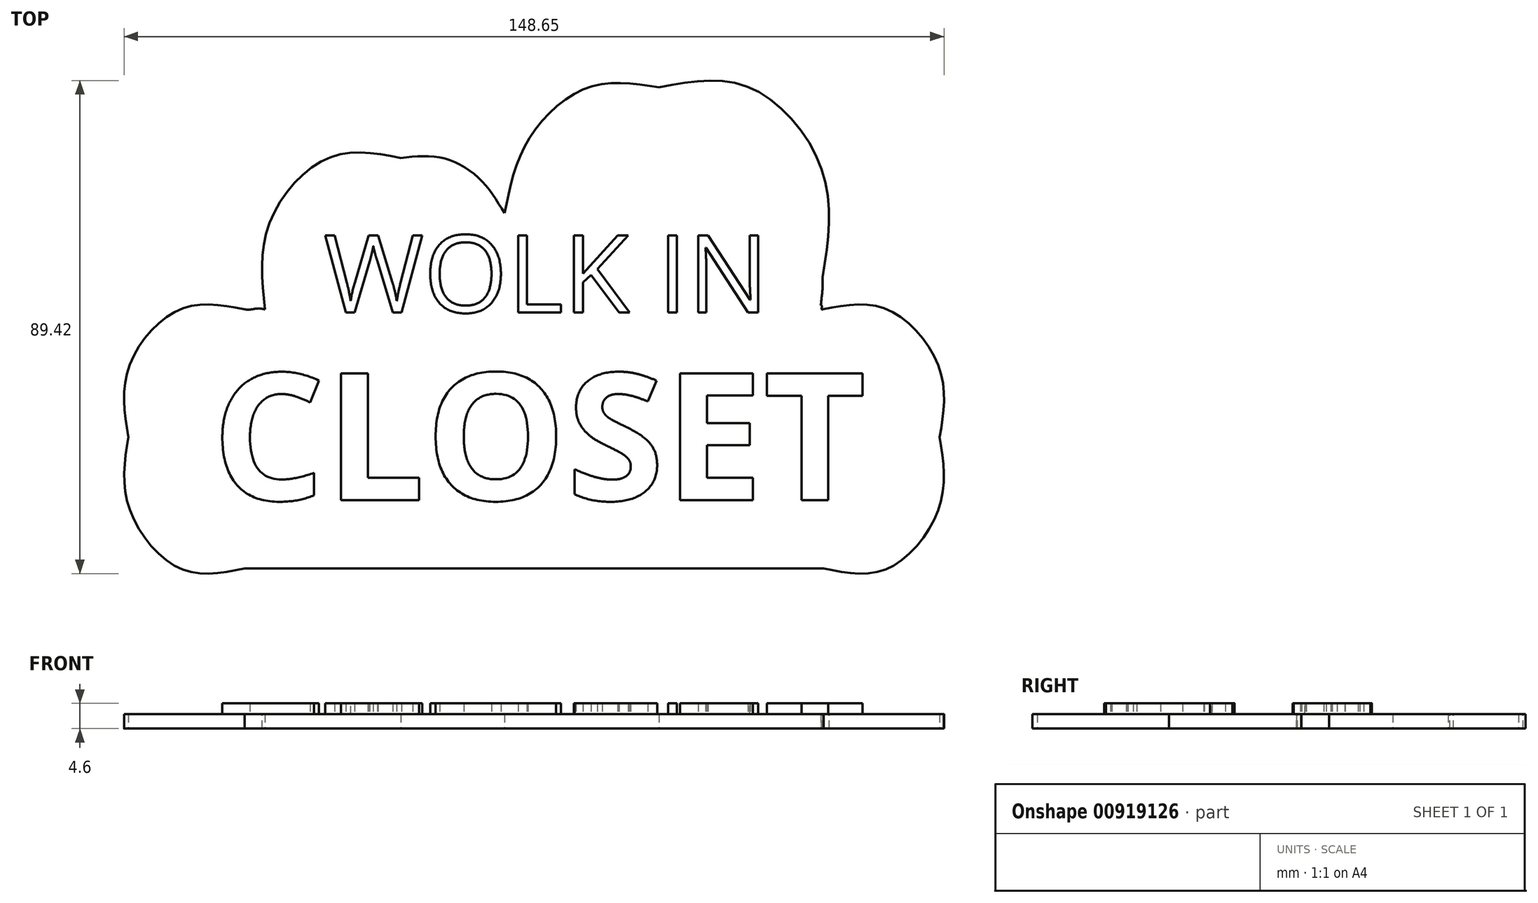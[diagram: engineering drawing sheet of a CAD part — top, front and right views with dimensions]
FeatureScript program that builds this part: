
annotation { "Feature Type Name" : "Feature", "Feature Type Description" : "" }
export const myFeature = defineFeature(function(context is Context, id is Id, definition is map)
    precondition{}
    {
        {
            var Q0;
            Q0=qCreatedBy(makeId("Top.planeOp"),FACE);
            var sketch = newSketch(context, id + "F0", { "sketchPlane" : qUnion([Q0])});
            skLineSegment(sketch, "E0", {"start": v(52.48, -43.62) * mm, "end": v(-52.48, -43.62) * mm});
            skFitSpline(sketch, "E1", {"points": [v(73.54, -19.78) * mm, v(73.54, -32.22) * mm, v(64.14, -43.62) * mm, v(52.48, -43.62) * mm]});
            skFitSpline(sketch, "E2", {"points": [v(-52.48, -43.62) * mm, v(-64.14, -43.62) * mm, v(-73.54, -32.22) * mm, v(-73.54, -19.78) * mm]});
            skFitSpline(sketch, "E3", {"points": [v(-73.54, -19.78) * mm, v(-73.54, -7.34) * mm, v(-64.14, 3.37) * mm, v(-52.48, 3.37) * mm]});
            skFitSpline(sketch, "E4", {"points": [v(-52.48, 3.37) * mm, v(-51.18, 3.37) * mm, v(-50.05, 3.54) * mm, v(-48.75, 3.37) * mm]});
            skFitSpline(sketch, "E5", {"points": [v(-48.75, 3.37) * mm, v(-48.1, 18.57) * mm, v(-37.25, 30.83) * mm, v(-24.13, 30.83) * mm]});
            skFitSpline(sketch, "E6", {"points": [v(-24.13, 30.83) * mm, v(-16.52, 30.83) * mm, v(-9.88, 27.03) * mm, v(-5.35, 20.82) * mm]});
            skFitSpline(sketch, "E7", {"points": [v(-5.35, 20.82) * mm, v(-1.13, 33.94) * mm, v(9.88, 43.62) * mm, v(22.68, 43.62) * mm]});
            skFitSpline(sketch, "E8", {"points": [v(22.68, 43.62) * mm, v(39.04, 43.62) * mm, v(52.32, 28.24) * mm, v(52.32, 9.24) * mm]});
            skFitSpline(sketch, "E9", {"points": [v(52.32, 9.24) * mm, v(52.32, 7.51) * mm, v(52.16, 5.61) * mm, v(52, 4.06) * mm]});
            skFitSpline(sketch, "E10", {"points": [v(52, 4.06) * mm, v(52.16, 4.06) * mm, v(52.16, 3.37) * mm, v(52.32, 3.37) * mm]});
            skFitSpline(sketch, "E11", {"points": [v(52.32, 3.37) * mm, v(63.98, 3.37) * mm, v(73.54, -7.51) * mm, v(73.54, -19.78) * mm]});
            skSolve(sketch);
        }
        {
            var Q0;
            Q0 = qSketchRegion(id + "F0", true);
            extrude(context, id + "F1", {"entities" : qUnion([Q0]), "depth" : 2.6 * mm, "offsetDistance" : 25 * mm});
        }
        {
            var Q0;
            Q0=makeQuery(id+"F1.opExtrude","CAP_FACE",FACE,{"disambiguationData":[OSD([sQuery(id+"F0.wireOp",EDGE,"E0"),sQuery(id+"F0.wireOp",EDGE,"E1"),sQuery(id+"F0.wireOp",EDGE,"E2"),sQuery(id+"F0.wireOp",EDGE,"E3"),sQuery(id+"F0.wireOp",EDGE,"E4"),sQuery(id+"F0.wireOp",EDGE,"E5"),sQuery(id+"F0.wireOp",EDGE,"E6"),sQuery(id+"F0.wireOp",EDGE,"E7"),sQuery(id+"F0.wireOp",EDGE,"E8"),sQuery(id+"F0.wireOp",EDGE,"E9"),sQuery(id+"F0.wireOp",EDGE,"E10"),sQuery(id+"F0.wireOp",EDGE,"E11")])],"isStart":false});
            var sketch = newSketch(context, id + "F2", { "sketchPlane" : qUnion([Q0])});
            skText(sketch, "E12", { "text": "WOLK IN", "fontName": "OpenSans-Regular.ttf"});
            skText(sketch, "E13", { "text": "CLOSET", "fontName": "OpenSans-Bold.ttf"});
            const initialGuessF2  = {"E12": [-0.0381, 0.00283, 1, 0, 0.01406], "E13": [-0.05837, -0.03121, 1, 0, 0.02315]};
            skSetInitialGuess(sketch, initialGuessF2);
            skSolve(sketch);
        }
        {
            var Q0;
            Q0 = qSketchRegion(id + "F2", true);
            extrude(context, id + "F3", {"entities" : qUnion([Q0]), "operationType" : NewBodyOperationType.ADD, "depth" : 2 * mm, "offsetDistance" : 25 * mm});
        }
    });
